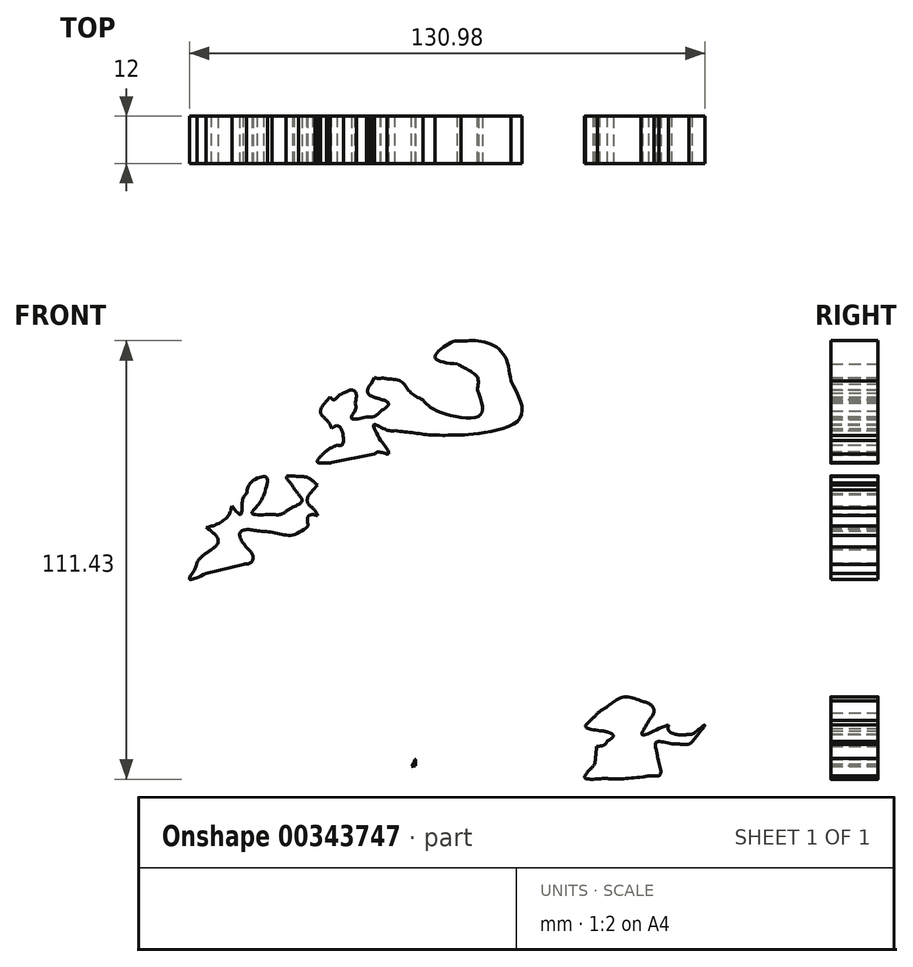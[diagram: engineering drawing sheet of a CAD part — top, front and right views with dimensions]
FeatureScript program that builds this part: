
annotation { "Feature Type Name" : "Feature", "Feature Type Description" : "" }
export const myFeature = defineFeature(function(context is Context, id is Id, definition is map)
    precondition{}
    {
        {
            var Q0;
            Q0=qCreatedBy(makeId("Front.planeOp"),FACE);
            var sketch = newSketch(context, id + "F0", { "sketchPlane" : qUnion([Q0])});
            skFitSpline(sketch, "E0", {"points": [v(1.14, 24.06) * mm, v(0.1, 25.49) * mm, v(-0.07, 26.06) * mm, v(-1.13, 27.51) * mm]});
            skFitSpline(sketch, "E1", {"points": [v(-1.13, 27.51) * mm, v(-2.47, 28.92) * mm, v(-2.34, 30.47) * mm, v(-1.07, 32.12) * mm]});
            skFitSpline(sketch, "E2", {"points": [v(-28.21, 22.55) * mm, v(-25.66, 23.36) * mm, v(-22.71, 25.44) * mm, v(-21.61, 28.33) * mm]});
            skLineSegment(sketch, "E3", {"start": v(0.05, 33.42) * mm, "end": v(-1.07, 32.12) * mm});
            skFitSpline(sketch, "E4", {"points": [v(-22.4, 29.05) * mm, v(-19.43, 25.95) * mm, v(-19.02, 29.42) * mm, v(-17.96, 31.23) * mm]});
            skFitSpline(sketch, "E5", {"points": [v(-17.97, 31.2) * mm, v(-16.79, 34.1) * mm, v(-12.98, 35.4) * mm, v(-13.57, 30.94) * mm]});
            skFitSpline(sketch, "E6", {"points": [v(-13.57, 30.94) * mm, v(-14.9, 28.47) * mm, v(-16.55, 26.25) * mm, v(-11.56, 25.95) * mm]});
            skFitSpline(sketch, "E7", {"points": [v(-11.56, 25.95) * mm, v(-9.3, 25.93) * mm, v(-7.7, 26.84) * mm, v(-6.15, 27.8) * mm]});
            skFitSpline(sketch, "E8", {"points": [v(-6.15, 27.8) * mm, v(-3.9, 29.27) * mm, v(-4.6, 30.78) * mm, v(-5.74, 32.3) * mm]});
            skFitSpline(sketch, "E9", {"points": [v(-5.74, 32.3) * mm, v(-6.82, 33.9) * mm, v(-7.87, 35.49) * mm, v(-4.77, 35.52) * mm]});
            skFitSpline(sketch, "E10", {"points": [v(-4.77, 35.52) * mm, v(-3.47, 35.5) * mm, v(-2.12, 35.16) * mm, v(-0.6, 33.92) * mm]});
            skFitSpline(sketch, "E11", {"points": [v(1.94, 22.87) * mm, v(2.42, 24.17) * mm, v(-1.9, 25.76) * mm, v(-2.01, 21.73) * mm]});
            skFitSpline(sketch, "E12", {"points": [v(-1.31, 23.76) * mm, v(-6.4, 20.69) * mm, v(-10.79, 21.24) * mm, v(-15.19, 21.7) * mm]});
            skFitSpline(sketch, "E13", {"points": [v(-15.19, 21.7) * mm, v(-18.42, 22) * mm, v(-19.73, 20.9) * mm, v(-18.08, 17.6) * mm]});
            skFitSpline(sketch, "E14", {"points": [v(-18.08, 17.6) * mm, v(-16.35, 15.49) * mm, v(-16.74, 13.79) * mm, v(-18.78, 13.26) * mm]});
            skFitSpline(sketch, "E15", {"points": [v(-28.21, 10.92) * mm, v(-32.49, 9.45) * mm, v(-31.27, 11.72) * mm, v(-30.6, 13.6) * mm]});
            skFitSpline(sketch, "E16", {"points": [v(-30.6, 13.6) * mm, v(-29.9, 14.67) * mm, v(-28.31, 16.04) * mm, v(-26.82, 17.03) * mm]});
            skFitSpline(sketch, "E17", {"points": [v(-26.82, 17.03) * mm, v(-25.2, 18.79) * mm, v(-25.82, 20.64) * mm, v(-28.21, 22.55) * mm]});
            skLineSegment(sketch, "E18", {"start": v(-18.78, 13.26) * mm, "end": v(-28.21, 10.92) * mm});
            skFitSpline(sketch, "E19", {"points": [v(23.55, -38.24) * mm, v(25, -37.91) * mm, v(26.75, -37.57) * mm, v(27.65, -36.54) * mm]});
            skFitSpline(sketch, "E20", {"points": [v(27.65, -36.54) * mm, v(29.18, -35.14) * mm, v(27.43, -34.16) * mm, v(25.81, -33.9) * mm]});
            skFitSpline(sketch, "E21", {"points": [v(25.81, -33.9) * mm, v(22.07, -32.8) * mm, v(23.6, -31.09) * mm, v(25.19, -29.37) * mm]});
            skFitSpline(sketch, "E22", {"points": [v(25.19, -29.37) * mm, v(28.5, -27.13) * mm, v(31.94, -25.33) * mm, v(36.23, -26.33) * mm]});
            skFitSpline(sketch, "E23", {"points": [v(36.23, -26.33) * mm, v(38.79, -27.39) * mm, v(39.55, -29) * mm, v(38.26, -31.23) * mm]});
            skFitSpline(sketch, "E24", {"points": [v(38.26, -31.23) * mm, v(37.1, -33.25) * mm, v(36.49, -34.9) * mm, v(40.7, -33.36) * mm]});
            skFitSpline(sketch, "E25", {"points": [v(18.4, -2.83) * mm, v(16.18, -5.15) * mm, v(14.83, -7.55) * mm, v(13.77, -9.98) * mm]});
            skFitSpline(sketch, "E26", {"points": [v(13.77, -9.98) * mm, v(11.86, -14.86) * mm, v(14.9, -19.46) * mm, v(20.15, -14.28) * mm]});
            skFitSpline(sketch, "E27", {"points": [v(20.15, -14.28) * mm, v(21.12, -13.45) * mm, v(25.75, -10.75) * mm, v(25.67, -17.7) * mm]});
            skFitSpline(sketch, "E28", {"points": [v(25.67, -17.7) * mm, v(25.79, -22.3) * mm, v(23.7, -27.14) * mm, v(19.9, -24.84) * mm]});
            skFitSpline(sketch, "E29", {"points": [v(19.9, -24.84) * mm, v(17.7, -21.55) * mm, v(15.28, -22.55) * mm, v(14.3, -25.93) * mm]});
            skFitSpline(sketch, "E30", {"points": [v(14.3, -25.93) * mm, v(12.15, -30.8) * mm, v(13.4, -35.42) * mm, v(14.12, -40.07) * mm]});
            skLineSegment(sketch, "E31", {"start": v(40.7, -33.36) * mm, "end": v(43.35, -32.38) * mm});
            skFitSpline(sketch, "E32", {"points": [v(42.7, -22.75) * mm, v(45.12, -25.4) * mm, v(47.51, -25.97) * mm, v(44.38, -29.35) * mm]});
            skFitSpline(sketch, "E33", {"points": [v(44.38, -29.35) * mm, v(43.46, -30.53) * mm, v(43.19, -31.57) * mm, v(43.33, -32.07) * mm]});
            skFitSpline(sketch, "E34", {"points": [v(24.5, -42.3) * mm, v(24.89, -36.28) * mm, v(23.55, -38.65) * mm, v(19.44, -38.92) * mm]});
            skLineSegment(sketch, "E35", {"start": v(42.7, -22.75) * mm, "end": v(38.42, -15.9) * mm});
            skLineSegment(sketch, "E36", {"start": v(19.44, -38.92) * mm, "end": v(14.12, -40.07) * mm});
            skFitSpline(sketch, "E37", {"points": [v(-57.66, -27.84) * mm, v(-56.83, -27.71) * mm, v(-56.43, -28.3) * mm, v(-55.7, -28.96) * mm]});
            skFitSpline(sketch, "E38", {"points": [v(-55.7, -28.96) * mm, v(-53.84, -30.14) * mm, v(-53.08, -28.29) * mm, v(-52.57, -26.7) * mm]});
            skFitSpline(sketch, "E39", {"points": [v(-52.57, -26.7) * mm, v(-51.9, -22.24) * mm, v(-47.4, -21.83) * mm, v(-45.76, -27.88) * mm]});
            skFitSpline(sketch, "E40", {"points": [v(-45.76, -27.88) * mm, v(-45.37, -29.91) * mm, v(-44.91, -31.94) * mm, v(-46.05, -34.12) * mm]});
            skFitSpline(sketch, "E41", {"points": [v(-46.05, -34.12) * mm, v(-47.96, -37.99) * mm, v(-49, -36.75) * mm, v(-51.2, -35.17) * mm]});
            skFitSpline(sketch, "E42", {"points": [v(-51.2, -35.17) * mm, v(-53.77, -33.8) * mm, v(-55.64, -36.26) * mm, v(-54.72, -39.2) * mm]});
            skFitSpline(sketch, "E43", {"points": [v(-54.72, -39.2) * mm, v(-53.79, -43.82) * mm, v(-50.18, -45.8) * mm, v(-45.57, -46.1) * mm]});
            skFitSpline(sketch, "E44", {"points": [v(-69.42, -19.21) * mm, v(-67.99, -19) * mm, v(-64.35, -18.07) * mm, v(-63.82, -22.72) * mm]});
            skFitSpline(sketch, "E45", {"points": [v(-63.82, -22.72) * mm, v(-63.96, -26.57) * mm, v(-64.82, -30.79) * mm, v(-59.94, -29.65) * mm]});
            skFitSpline(sketch, "E46", {"points": [v(-59.94, -29.65) * mm, v(-57.46, -29.08) * mm, v(-57.02, -27.71) * mm, v(-58.51, -25.34) * mm]});
            skFitSpline(sketch, "E47", {"points": [v(-41.95, -45.86) * mm, v(-47.26, -46.09) * mm, v(-45.63, -45.63) * mm, v(-46.62, -49.37) * mm]});
            skFitSpline(sketch, "E48", {"points": [v(-46.62, -49.37) * mm, v(-47.5, -51.76) * mm, v(-49.68, -51.73) * mm, v(-51.5, -52.04) * mm]});
            skFitSpline(sketch, "E49", {"points": [v(-62.53, -52.33) * mm, v(-65.2, -52.76) * mm, v(-64.29, -50.13) * mm, v(-63.4, -47.53) * mm]});
            skLineSegment(sketch, "E50", {"start": v(-62.53, -52.33) * mm, "end": v(-51.5, -52.04) * mm});
            skFitSpline(sketch, "E51", {"points": [v(-60.23, -42.06) * mm, v(-58.84, -39.3) * mm, v(-62.05, -38.54) * mm, v(-63.36, -38.13) * mm]});
            skFitSpline(sketch, "E52", {"points": [v(-63.36, -38.13) * mm, v(-70.72, -37.73) * mm, v(-75.6, -35.42) * mm, v(-76.3, -33.79) * mm]});
            skFitSpline(sketch, "E53", {"points": [v(-76.3, -33.79) * mm, v(-77.61, -32.87) * mm, v(-77.54, -30.3) * mm, v(-77.19, -27.4) * mm]});
            skFitSpline(sketch, "E54", {"points": [v(-77.19, -27.4) * mm, v(-76.92, -23.48) * mm, v(-74.25, -20.8) * mm, v(-69.42, -19.21) * mm]});
            skLineSegment(sketch, "E55", {"start": v(-60.23, -42.06) * mm, "end": v(-63.4, -47.53) * mm});
            skFitSpline(sketch, "E56", {"points": [v(-3.4, -16.07) * mm, v(9.82, 0.5) * mm, v(23.69, 2.44) * mm, v(38.45, -15.93) * mm]});
            skFitSpline(sketch, "E57", {"points": [v(-12, -8.72) * mm, v(-14.23, -11.04) * mm, v(-15.58, -13.44) * mm, v(-16.65, -15.86) * mm]});
            skFitSpline(sketch, "E58", {"points": [v(-16.65, -15.86) * mm, v(-18.57, -20.74) * mm, v(-15.54, -25.35) * mm, v(-10.27, -20.19) * mm]});
            skFitSpline(sketch, "E59", {"points": [v(-10.3, -20.21) * mm, v(-9.33, -19.38) * mm, v(-4.7, -16.7) * mm, v(-4.79, -23.64) * mm]});
            skFitSpline(sketch, "E60", {"points": [v(-4.79, -23.57) * mm, v(-4.64, -28.17) * mm, v(-6.7, -33.01) * mm, v(-10.51, -30.74) * mm]});
            skFitSpline(sketch, "E61", {"points": [v(-10.51, -30.74) * mm, v(-12.71, -27.45) * mm, v(-15.14, -28.45) * mm, v(-16.1, -31.83) * mm]});
            skFitSpline(sketch, "E62", {"points": [v(-16.1, -31.83) * mm, v(-18.26, -36.7) * mm, v(-17.01, -41.32) * mm, v(-16.3, -45.97) * mm]});
            skFitSpline(sketch, "E63", {"points": [v(-35.25, -28.72) * mm, v(-34.42, -28.6) * mm, v(-34.02, -29.19) * mm, v(-33.3, -29.84) * mm]});
            skFitSpline(sketch, "E64", {"points": [v(-33.3, -29.84) * mm, v(-31.43, -31.02) * mm, v(-30.67, -29.17) * mm, v(-30.16, -27.59) * mm]});
            skFitSpline(sketch, "E65", {"points": [v(-30.16, -27.59) * mm, v(-29.49, -23.12) * mm, v(-24.99, -22.7) * mm, v(-23.35, -28.76) * mm]});
            skFitSpline(sketch, "E66", {"points": [v(-23.35, -28.76) * mm, v(-22.97, -30.79) * mm, v(-22.5, -32.82) * mm, v(-23.64, -35) * mm]});
            skFitSpline(sketch, "E67", {"points": [v(-23.64, -35) * mm, v(-25.55, -38.87) * mm, v(-26.6, -37.63) * mm, v(-28.78, -36.04) * mm]});
            skFitSpline(sketch, "E68", {"points": [v(-28.78, -36.04) * mm, v(-31.36, -34.69) * mm, v(-33.23, -37.14) * mm, v(-32.31, -40.07) * mm]});
            skFitSpline(sketch, "E69", {"points": [v(-32.31, -40.05) * mm, v(-31.37, -44.67) * mm, v(-27.75, -46.64) * mm, v(-23.15, -46.94) * mm]});
            skFitSpline(sketch, "E70", {"points": [v(-36.2, -26.19) * mm, v(-37.7, -23.46) * mm, v(-36.76, -22.14) * mm, v(-33.81, -21.97) * mm]});
            skFitSpline(sketch, "E71", {"points": [v(-33.81, -21.97) * mm, v(-20.6, -5.4) * mm, v(-6.73, -3.45) * mm, v(8.03, -21.83) * mm]});
            skLineSegment(sketch, "E72", {"start": v(-16.3, -45.97) * mm, "end": v(-19.51, -46.66) * mm});
            skFitSpline(sketch, "E73", {"points": [v(-36.2, -26.19) * mm, v(-35.25, -28.72) * mm], "startDerivative": vector(2.95, -4.94) * mm, "endDerivative": vector(1.45, -2.14) * mm});
            skFitSpline(sketch, "E74", {"points": [v(-23.27, -46.93) * mm, v(-19.51, -46.66) * mm], "startDerivative": vector(4.17, -0.3) * mm, "endDerivative": vector(3.62, 0.8) * mm});
            skFitSpline(sketch, "E75", {"points": [v(69.58, -33.38) * mm, v(71.03, -33.05) * mm, v(72.79, -32.71) * mm, v(73.69, -31.67) * mm]});
            skFitSpline(sketch, "E76", {"points": [v(73.69, -31.67) * mm, v(75.22, -30.28) * mm, v(73.46, -29.3) * mm, v(71.85, -29.04) * mm]});
            skFitSpline(sketch, "E77", {"points": [v(71.85, -29.04) * mm, v(68.1, -27.93) * mm, v(69.64, -26.22) * mm, v(71.22, -24.51) * mm]});
            skFitSpline(sketch, "E78", {"points": [v(71.22, -24.51) * mm, v(74.53, -22.27) * mm, v(77.97, -20.46) * mm, v(82.27, -21.46) * mm]});
            skFitSpline(sketch, "E79", {"points": [v(82.27, -21.46) * mm, v(84.82, -22.53) * mm, v(85.58, -24.14) * mm, v(84.3, -26.37) * mm]});
            skFitSpline(sketch, "E80", {"points": [v(84.3, -26.37) * mm, v(83.13, -28.4) * mm, v(82.52, -30.04) * mm, v(86.74, -28.5) * mm]});
            skLineSegment(sketch, "E81", {"start": v(86.74, -28.5) * mm, "end": v(89.39, -27.52) * mm});
            skLineSegment(sketch, "E82", {"start": v(89.39, -27.52) * mm, "end": v(86.74, -28.5) * mm});
            skFitSpline(sketch, "E83", {"points": [v(89.37, -27.2) * mm, v(89.28, -29) * mm, v(92.1, -30.1) * mm, v(94.42, -29.92) * mm]});
            skFitSpline(sketch, "E84", {"points": [v(94.42, -29.92) * mm, v(95.43, -29.76) * mm, v(98.43, -27.58) * mm, v(95.26, -31.72) * mm]});
            skFitSpline(sketch, "E85", {"points": [v(95.26, -31.72) * mm, v(94.46, -32.44) * mm, v(91.88, -32.42) * mm, v(90.16, -32.43) * mm]});
            skFitSpline(sketch, "E86", {"points": [v(90.16, -32.43) * mm, v(86.02, -32.01) * mm, v(86.15, -34) * mm, v(86.49, -36.1) * mm]});
            skFitSpline(sketch, "E87", {"points": [v(86.49, -36.1) * mm, v(87.05, -40.27) * mm, v(84.88, -40.52) * mm, v(82.73, -40.78) * mm]});
            skFitSpline(sketch, "E88", {"points": [v(82.73, -40.78) * mm, v(76.03, -41.3) * mm, v(73.09, -41.19) * mm, v(70.2, -41.36) * mm]});
            skFitSpline(sketch, "E89", {"points": [v(70.2, -41.36) * mm, v(67.9, -40.91) * mm, v(69.25, -38.94) * mm, v(70.53, -37.44) * mm]});
            skFitSpline(sketch, "E90", {"points": [v(70.53, -37.44) * mm, v(70.93, -31.42) * mm, v(69.59, -33.78) * mm, v(65.48, -34.05) * mm]});
            skLineSegment(sketch, "E91", {"start": v(43.33, -32.07) * mm, "end": v(43.35, -32.38) * mm});
            skFitSpline(sketch, "E92", {"points": [v(-69.33, 19.2) * mm, v(-66.78, 20.02) * mm, v(-63.84, 22.1) * mm, v(-62.74, 25) * mm]});
            skFitSpline(sketch, "E93", {"points": [v(-62.74, 35.45) * mm, v(-62.46, 30.66) * mm, v(-64.3, 31.89) * mm, v(-66.25, 33.44) * mm]});
            skFitSpline(sketch, "E94", {"points": [v(-66.25, 33.44) * mm, v(-68.63, 34.88) * mm, v(-69.96, 33.7) * mm, v(-70.77, 31.22) * mm]});
            skFitSpline(sketch, "E95", {"points": [v(-70.77, 31.22) * mm, v(-72.11, 28.7) * mm, v(-71.32, 25.2) * mm, v(-67.47, 27.03) * mm]});
            skFitSpline(sketch, "E96", {"points": [v(-67.47, 27.03) * mm, v(-66.37, 27.88) * mm, v(-65.04, 27.46) * mm, v(-63.45, 25.58) * mm]});
            skFitSpline(sketch, "E97", {"points": [v(-85.3, 36) * mm, v(-85.04, 39.47) * mm, v(-78.71, 40.43) * mm, v(-76.06, 38.9) * mm]});
            skFitSpline(sketch, "E98", {"points": [v(-76.06, 38.9) * mm, v(-73.53, 36.41) * mm, v(-70.77, 35.17) * mm, v(-67.23, 38.16) * mm]});
            skFitSpline(sketch, "E99", {"points": [v(-67.23, 38.16) * mm, v(-65.9, 39.02) * mm, v(-64.94, 40.17) * mm, v(-61.89, 39.68) * mm]});
            skLineSegment(sketch, "E100", {"start": v(-63.84, 39.77) * mm, "end": v(-62.74, 35.45) * mm});
            skLineSegment(sketch, "E101", {"start": v(-62.74, 35.45) * mm, "end": v(-63.84, 39.77) * mm});
            skFitSpline(sketch, "E102", {"points": [v(-69.32, 19.2) * mm, v(-74.17, 19.65) * mm, v(-75.13, 21.04) * mm, v(-77.62, 23.3) * mm]});
            skFitSpline(sketch, "E103", {"points": [v(-77.62, 23.3) * mm, v(-79.5, 25) * mm, v(-81.46, 25.23) * mm, v(-83.41, 25.38) * mm]});
            skFitSpline(sketch, "E104", {"points": [v(-83.41, 25.38) * mm, v(-85.23, 25.36) * mm, v(-85.68, 26.46) * mm, v(-85.86, 27.77) * mm]});
            skFitSpline(sketch, "E105", {"points": [v(-85.86, 27.77) * mm, v(-87.84, 28.9) * mm, v(-87.15, 30.61) * mm, v(-86.19, 32.37) * mm]});
            skFitSpline(sketch, "E106", {"points": [v(-86.19, 32.37) * mm, v(-85.6, 32.96) * mm, v(-85.27, 34.09) * mm, v(-85.3, 36) * mm]});
            skLineSegment(sketch, "E107", {"start": v(-63.45, 25.58) * mm, "end": v(-62.74, 25) * mm});
            skFitSpline(sketch, "E108", {"points": [v(-54.6, 57.36) * mm, v(-54.3, 52.58) * mm, v(-56.15, 53.8) * mm, v(-58.1, 55.35) * mm]});
            skFitSpline(sketch, "E109", {"points": [v(-58.1, 55.35) * mm, v(-60.49, 56.8) * mm, v(-61.81, 55.61) * mm, v(-62.62, 53.13) * mm]});
            skFitSpline(sketch, "E110", {"points": [v(-62.62, 53.13) * mm, v(-63.96, 50.6) * mm, v(-63.17, 47.12) * mm, v(-59.32, 48.94) * mm]});
            skFitSpline(sketch, "E111", {"points": [v(-59.32, 48.94) * mm, v(-58.22, 49.8) * mm, v(-56.9, 49.37) * mm, v(-55.3, 47.5) * mm]});
            skFitSpline(sketch, "E112", {"points": [v(-55.3, 47.5) * mm, v(-52.26, 44.48) * mm, v(-51.94, 47.96) * mm, v(-50.93, 49.8) * mm]});
            skFitSpline(sketch, "E113", {"points": [v(-50.93, 49.8) * mm, v(-49.73, 52.68) * mm, v(-45.92, 53.96) * mm, v(-46.53, 49.5) * mm]});
            skFitSpline(sketch, "E114", {"points": [v(-46.53, 49.5) * mm, v(-47.87, 47.03) * mm, v(-49.51, 44.82) * mm, v(-44.52, 44.51) * mm]});
            skFitSpline(sketch, "E115", {"points": [v(-44.52, 44.51) * mm, v(-42.26, 44.5) * mm, v(-40.67, 45.4) * mm, v(-39.12, 46.37) * mm]});
            skFitSpline(sketch, "E116", {"points": [v(-39.12, 46.37) * mm, v(-36.86, 47.83) * mm, v(-37.56, 49.34) * mm, v(-38.7, 50.86) * mm]});
            skFitSpline(sketch, "E117", {"points": [v(-38.7, 50.86) * mm, v(-39.79, 52.46) * mm, v(-40.84, 54.05) * mm, v(-37.73, 54.08) * mm]});
            skFitSpline(sketch, "E118", {"points": [v(-37.73, 54.08) * mm, v(-36.44, 54.06) * mm, v(-35.08, 53.72) * mm, v(-33.57, 52.48) * mm]});
            skFitSpline(sketch, "E119", {"points": [v(-33.57, 52.48) * mm, v(-32.15, 51.03) * mm, v(-30.92, 52.07) * mm, v(-29.67, 52.75) * mm]});
            skFitSpline(sketch, "E120", {"points": [v(-29.67, 52.75) * mm, v(-27.48, 53.53) * mm, v(-26.5, 52.69) * mm, v(-26.72, 50.24) * mm]});
            skFitSpline(sketch, "E121", {"points": [v(-26.72, 50.24) * mm, v(-26.66, 48.59) * mm, v(-27.66, 46.4) * mm, v(-23.88, 46.64) * mm]});
            skFitSpline(sketch, "E122", {"points": [v(-23.88, 46.64) * mm, v(-22.02, 46.77) * mm, v(-20.98, 47.37) * mm, v(-20.22, 48.14) * mm]});
            skFitSpline(sketch, "E123", {"points": [v(-20.22, 48.14) * mm, v(-18.23, 50.1) * mm, v(-20.23, 51.2) * mm, v(-21.84, 51.66) * mm]});
            skFitSpline(sketch, "E124", {"points": [v(-21.84, 51.66) * mm, v(-23.44, 52.65) * mm, v(-23.47, 53.84) * mm, v(-22.73, 55.11) * mm]});
            skFitSpline(sketch, "E125", {"points": [v(-59.09, 60.1) * mm, v(-57.75, 60.95) * mm, v(-56.79, 62.09) * mm, v(-53.74, 61.58) * mm]});
            skFitSpline(sketch, "E126", {"points": [v(-53.74, 61.58) * mm, v(-52.62, 61.5) * mm, v(-51.52, 61.31) * mm, v(-50.25, 62.53) * mm]});
            skFitSpline(sketch, "E127", {"points": [v(-50.25, 62.53) * mm, v(-49.24, 63.21) * mm, v(-47.99, 63.48) * mm, v(-46.26, 62.9) * mm]});
            skFitSpline(sketch, "E128", {"points": [v(-46.26, 62.9) * mm, v(-44.83, 62.57) * mm, v(-43.42, 62.55) * mm, v(-42.07, 63.23) * mm]});
            skFitSpline(sketch, "E129", {"points": [v(-42.07, 63.23) * mm, v(-40.82, 63.9) * mm, v(-39.68, 63.71) * mm, v(-38.59, 63.12) * mm]});
            skFitSpline(sketch, "E130", {"points": [v(-38.59, 63.12) * mm, v(-37.5, 62.37) * mm, v(-36.27, 62.22) * mm, v(-34.87, 62.73) * mm]});
            skFitSpline(sketch, "E131", {"points": [v(-34.87, 62.73) * mm, v(-33.94, 62.82) * mm, v(-33.12, 63.23) * mm, v(-31.82, 62.05) * mm]});
            skFitSpline(sketch, "E132", {"points": [v(-31.82, 62.05) * mm, v(-30.69, 61.53) * mm, v(-29.75, 60.88) * mm, v(-27.72, 60.96) * mm]});
            skFitSpline(sketch, "E133", {"points": [v(-27.72, 60.96) * mm, v(-25.7, 61.04) * mm, v(-24.83, 58.87) * mm, v(-23.24, 57.86) * mm]});
            skFitSpline(sketch, "E134", {"points": [v(-23.24, 57.86) * mm, v(-21.88, 56.72) * mm, v(-20.1, 56.56) * mm, v(-18.89, 56.27) * mm]});
            skLineSegment(sketch, "E135", {"start": v(-55.7, 61.68) * mm, "end": v(-54.6, 57.36) * mm});
            skLineSegment(sketch, "E136", {"start": v(-21.7, 56.97) * mm, "end": v(-22.73, 55.11) * mm});
            skFitSpline(sketch, "E137", {"points": [v(4.53, 46.62) * mm, v(3.5, 48.05) * mm, v(3.32, 48.62) * mm, v(2.25, 50.07) * mm]});
            skFitSpline(sketch, "E138", {"points": [v(2.25, 50.07) * mm, v(0.92, 51.49) * mm, v(1.05, 53.03) * mm, v(2.31, 54.68) * mm]});
            skLineSegment(sketch, "E139", {"start": v(2.31, 54.68) * mm, "end": v(3.43, 55.98) * mm});
            skFitSpline(sketch, "E140", {"points": [v(2.78, 56.5) * mm, v(4.2, 55.03) * mm, v(5.42, 56.07) * mm, v(6.68, 56.75) * mm]});
            skFitSpline(sketch, "E141", {"points": [v(6.68, 56.75) * mm, v(8.87, 57.53) * mm, v(9.84, 56.68) * mm, v(9.63, 54.24) * mm]});
            skFitSpline(sketch, "E142", {"points": [v(9.63, 54.24) * mm, v(9.69, 52.58) * mm, v(8.68, 50.4) * mm, v(12.47, 50.63) * mm]});
            skFitSpline(sketch, "E143", {"points": [v(12.47, 50.63) * mm, v(14.33, 50.76) * mm, v(15.37, 51.37) * mm, v(16.13, 52.14) * mm]});
            skFitSpline(sketch, "E144", {"points": [v(16.13, 52.14) * mm, v(18.12, 54.1) * mm, v(16.12, 55.19) * mm, v(14.5, 55.65) * mm]});
            skFitSpline(sketch, "E145", {"points": [v(14.5, 55.65) * mm, v(12.91, 56.65) * mm, v(12.88, 57.83) * mm, v(13.62, 59.1) * mm]});
            skFitSpline(sketch, "E146", {"points": [v(13.48, 61.6) * mm, v(14.92, 60.56) * mm, v(16.7, 60.53) * mm, v(17.94, 60.33) * mm]});
            skFitSpline(sketch, "E147", {"points": [v(17.5, 60.4) * mm, v(21.55, 59.54) * mm, v(23.45, 57.15) * mm, v(26.88, 54.97) * mm]});
            skFitSpline(sketch, "E148", {"points": [v(26.88, 54.97) * mm, v(30.55, 52.13) * mm, v(41.32, 51.09) * mm, v(40.67, 57.57) * mm]});
            skFitSpline(sketch, "E149", {"points": [v(40.67, 57.57) * mm, v(40.68, 60.74) * mm, v(38.42, 62.57) * mm, v(35.62, 64.1) * mm]});
            skFitSpline(sketch, "E150", {"points": [v(35.62, 64.1) * mm, v(29.96, 65.87) * mm, v(34.24, 69.72) * mm, v(36.57, 69.92) * mm]});
            skFitSpline(sketch, "E151", {"points": [v(36.57, 69.92) * mm, v(41.6, 69.87) * mm, v(47.02, 67) * mm, v(49.15, 59.85) * mm]});
            skFitSpline(sketch, "E152", {"points": [v(49.15, 59.85) * mm, v(51.4, 50.18) * mm, v(38.78, 46.27) * mm, v(34.65, 46.06) * mm]});
            skFitSpline(sketch, "E153", {"points": [v(34.65, 46.06) * mm, v(28.95, 46.12) * mm, v(24.33, 46.65) * mm, v(19.7, 47.18) * mm]});
            skFitSpline(sketch, "E154", {"points": [v(19.7, 47.18) * mm, v(17.34, 47.5) * mm, v(14.39, 48.74) * mm, v(16.1, 44.76) * mm]});
            skFitSpline(sketch, "E155", {"points": [v(16.1, 44.76) * mm, v(18.07, 41.32) * mm, v(15.76, 41.78) * mm, v(14.54, 41.24) * mm]});
            skFitSpline(sketch, "E156", {"points": [v(3.66, 39.07) * mm, v(1.22, 38.94) * mm, v(-0.01, 39.32) * mm, v(1.13, 41) * mm]});
            skFitSpline(sketch, "E157", {"points": [v(1.13, 41) * mm, v(2.22, 42.02) * mm, v(3.55, 42.84) * mm, v(5.09, 43.52) * mm]});
            skFitSpline(sketch, "E158", {"points": [v(5.09, 43.52) * mm, v(6.44, 43.8) * mm, v(5.54, 48.3) * mm, v(2.04, 46.29) * mm]});
            skLineSegment(sketch, "E159", {"start": v(14.54, 41.24) * mm, "end": v(3.66, 39.07) * mm});
            skLineSegment(sketch, "E160", {"start": v(3.66, 39.07) * mm, "end": v(14.54, 41.24) * mm});
            skLineSegment(sketch, "E161", {"start": v(14.66, 60.97) * mm, "end": v(13.62, 59.1) * mm});
            skLineSegment(sketch, "E162", {"start": v(-0.6, 33.92) * mm, "end": v(0.05, 33.42) * mm});
            skSolve(sketch);
        }
        {
            var Q0;
            Q0=makeQuery(id+"F0.imprint","IMPRINT",FACE,{"disambiguationData":[TD([[makeQuery(id+"F0.imprint","IMPRINT",EDGE,{"derivedFrom":sQuery(id+"F0.wireOp",EDGE,"E37")}),-1.0]])]});
            var Q1;
            Q1=makeQuery(id+"F0.imprint","IMPRINT",FACE,{"disambiguationData":[TD([[makeQuery(id+"F0.imprint","IMPRINT",EDGE,{"derivedFrom":sQuery(id+"F0.wireOp",EDGE,"E57")}),-1.0]])]});
            var Q2;
            Q2=makeQuery(id+"F0.imprint","IMPRINT",FACE,{"disambiguationData":[TD([[makeQuery(id+"F0.imprint","IMPRINT",EDGE,{"derivedFrom":sQuery(id+"F0.wireOp",EDGE,"E19")}),1.0]])]});
            var Q3;
            Q3=makeQuery(id+"F0.imprint","IMPRINT",FACE,{"disambiguationData":[TD([[makeQuery(id+"F0.imprint","IMPRINT",EDGE,{"derivedFrom":sQuery(id+"F0.wireOp",EDGE,"E75")}),-1.0]])]});
            extrude(context, id + "F1", {"entities" : qUnion([Q0, Q1, Q2, Q3]), "depth" : 12 * mm});
        }
        {
            var Q0;
            Q0=makeQuery(id+"F0.imprint","IMPRINT",FACE,{"disambiguationData":[TD([[makeQuery(id+"F0.imprint","IMPRINT",EDGE,{"derivedFrom":sQuery(id+"F0.wireOp",EDGE,"E92")}),1.0]])]});
            var Q1;
            Q1=makeQuery(id+"F0.imprint","IMPRINT",FACE,{"disambiguationData":[TD([[makeQuery(id+"F0.imprint","IMPRINT",EDGE,{"derivedFrom":sQuery(id+"F0.wireOp",EDGE,"E108")}),1.0]])]});
            var Q2;
            Q2=makeQuery(id+"F0.imprint","IMPRINT",FACE,{"disambiguationData":[TD([[makeQuery(id+"F0.imprint","IMPRINT",EDGE,{"derivedFrom":sQuery(id+"F0.wireOp",EDGE,"E0")}),1.0]])]});
            var Q3;
            Q3=makeQuery(id+"F0.imprint","IMPRINT",FACE,{"disambiguationData":[TD([[makeQuery(id+"F0.imprint","IMPRINT",EDGE,{"derivedFrom":sQuery(id+"F0.wireOp",EDGE,"E137")}),-1.0]])]});
            extrude(context, id + "F2", {"entities" : qUnion([Q0, Q1, Q2, Q3]), "depth" : 12 * mm});
        }
    });
